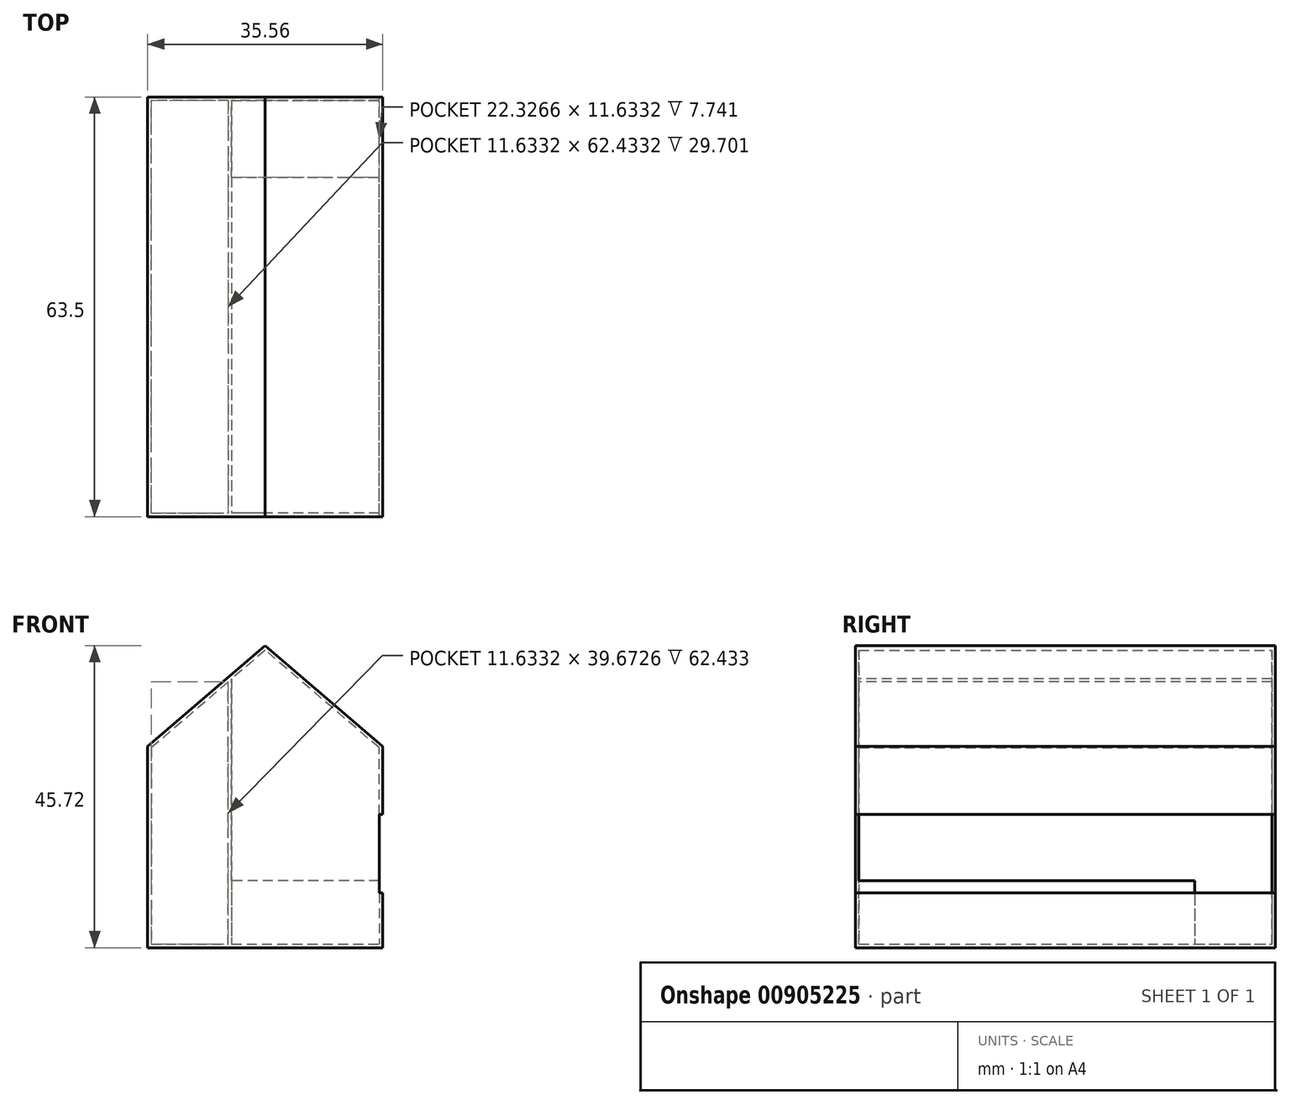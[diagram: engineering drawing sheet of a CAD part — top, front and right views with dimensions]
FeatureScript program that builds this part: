
annotation { "Feature Type Name" : "Feature", "Feature Type Description" : "" }
export const myFeature = defineFeature(function(context is Context, id is Id, definition is map)
    precondition{}
    {
        {
            var Q0;
            Q0=qCreatedBy(makeId("Front.planeOp"),FACE);
            var sketch = newSketch(context, id + "F0", { "sketchPlane" : qUnion([Q0])});
            skLineSegment(sketch, "E0", {"start": v(0, 0) * mm, "end": v(35.56, 0) * mm});
            skLineSegment(sketch, "E1", {"start": v(35.56, 0) * mm, "end": v(35.56, 8.27) * mm});
            skLineSegment(sketch, "E2", {"start": v(35.56, 30.48) * mm, "end": v(17.78, 45.72) * mm});
            skLineSegment(sketch, "E3", {"start": v(17.78, 45.72) * mm, "end": v(0, 30.48) * mm});
            skLineSegment(sketch, "E4", {"start": v(0, 30.48) * mm, "end": v(0, 0) * mm});
            skLineSegment(sketch, "E5.0", {"start": v(35.03, 30.23) * mm, "end": v(17.78, 45.02) * mm});
            skLineSegment(sketch, "E6.0", {"start": v(17.78, 45.02) * mm, "end": v(0.53, 30.23) * mm});
            skLineSegment(sketch, "E7.0", {"start": v(35.03, 0.53) * mm, "end": v(35.03, 8.27) * mm});
            skLineSegment(sketch, "E8.0", {"start": v(0.53, 30.23) * mm, "end": v(0.53, 0.53) * mm});
            skLineSegment(sketch, "E9.0", {"start": v(0.53, 0.53) * mm, "end": v(35.03, 0.53) * mm});
            skLineSegment(sketch, "E10", {"start": v(35.56, 8.27) * mm, "end": v(35.03, 8.27) * mm});
            skLineSegment(sketch, "E11", {"start": v(35.56, 20.14) * mm, "end": v(35.03, 20.14) * mm});
            skLineSegment(sketch, "E12.trimOffspring", {"start": v(35.03, 20.14) * mm, "end": v(35.03, 30.23) * mm});
            skLineSegment(sketch, "E13.trimOffspring", {"start": v(35.56, 20.14) * mm, "end": v(35.56, 30.48) * mm});
            skSolve(sketch);
        }
        {
            var Q0;
            Q0=makeQuery(id+"F0.imprint","IMPRINT",FACE,{"disambiguationData":[TD([[makeQuery(id+"F0.imprint","IMPRINT",EDGE,{"derivedFrom":sQuery(id+"F0.wireOp",EDGE,"E0")}),1.0]])]});
            extrude(context, id + "F1", {"entities" : qUnion([Q0]), "depth" : 63.5 * mm, "offsetDistance" : 25.4 * mm});
        }
        {
            var Q0;
            Q0=makeQuery(id+"F1.opExtrude","CAP_FACE",FACE,{"disambiguationData":[OSD([sQuery(id+"F0.wireOp",EDGE,"E0"),sQuery(id+"F0.wireOp",EDGE,"E1"),sQuery(id+"F0.wireOp",EDGE,"E2"),sQuery(id+"F0.wireOp",EDGE,"E3"),sQuery(id+"F0.wireOp",EDGE,"E4"),sQuery(id+"F0.wireOp",EDGE,"E5.0"),sQuery(id+"F0.wireOp",EDGE,"E6.0"),sQuery(id+"F0.wireOp",EDGE,"E7.0"),sQuery(id+"F0.wireOp",EDGE,"E8.0"),sQuery(id+"F0.wireOp",EDGE,"E9.0"),sQuery(id+"F0.wireOp",EDGE,"E10"),sQuery(id+"F0.wireOp",EDGE,"E11"),sQuery(id+"F0.wireOp",EDGE,"E12.trimOffspring"),sQuery(id+"F0.wireOp",EDGE,"E13.trimOffspring")])],"isStart":false});
            var sketch = newSketch(context, id + "F2", { "sketchPlane" : qUnion([Q0])});
            skLineSegment(sketch, "E14", {"start": v(35.03, 30.23) * mm, "end": v(17.78, 45.02) * mm});
            skLineSegment(sketch, "E15", {"start": v(17.78, 45.02) * mm, "end": v(0.53, 30.23) * mm});
            skLineSegment(sketch, "E16", {"start": v(0.53, 30.23) * mm, "end": v(0.53, 0.53) * mm});
            skLineSegment(sketch, "E17", {"start": v(0.53, 0.53) * mm, "end": v(35.03, 0.53) * mm});
            skLineSegment(sketch, "E18", {"start": v(35.03, 0.53) * mm, "end": v(35.03, 30.23) * mm});
            skSolve(sketch);
        }
        {
            var Q0;
            Q0 = qSketchRegion(id + "F2", true);
            extrude(context, id + "F3", {"entities" : qUnion([Q0]), "operationType" : NewBodyOperationType.ADD, "oppositeDirection" : true, "depth" : 0.53 * mm, "offsetDistance" : 25.4 * mm});
        }
        {
            var Q0;
            Q0=makeQuery(id+"F1.opExtrude","CAP_FACE",FACE,{"disambiguationData":[OSD([sQuery(id+"F0.wireOp",EDGE,"E0"),sQuery(id+"F0.wireOp",EDGE,"E1"),sQuery(id+"F0.wireOp",EDGE,"E2"),sQuery(id+"F0.wireOp",EDGE,"E3"),sQuery(id+"F0.wireOp",EDGE,"E4"),sQuery(id+"F0.wireOp",EDGE,"E5.0"),sQuery(id+"F0.wireOp",EDGE,"E6.0"),sQuery(id+"F0.wireOp",EDGE,"E7.0"),sQuery(id+"F0.wireOp",EDGE,"E8.0"),sQuery(id+"F0.wireOp",EDGE,"E9.0"),sQuery(id+"F0.wireOp",EDGE,"E10"),sQuery(id+"F0.wireOp",EDGE,"E11"),sQuery(id+"F0.wireOp",EDGE,"E12.trimOffspring"),sQuery(id+"F0.wireOp",EDGE,"E13.trimOffspring")])],"isStart":true});
            var sketch = newSketch(context, id + "F4", { "sketchPlane" : qUnion([Q0])});
            skLineSegment(sketch, "E19", {"start": v(-35.03, 0.53) * mm, "end": v(-35.03, 30.23) * mm});
            skLineSegment(sketch, "E20", {"start": v(-35.03, 30.23) * mm, "end": v(-17.78, 45.02) * mm});
            skLineSegment(sketch, "E21", {"start": v(-17.78, 45.02) * mm, "end": v(-0.53, 30.23) * mm});
            skLineSegment(sketch, "E22", {"start": v(-0.53, 30.23) * mm, "end": v(-0.53, 0.53) * mm});
            skLineSegment(sketch, "E23", {"start": v(-0.53, 0.53) * mm, "end": v(-35.03, 0.53) * mm});
            skSolve(sketch);
        }
        {
            var Q0;
            Q0 = qSketchRegion(id + "F4", true);
            extrude(context, id + "F5", {"entities" : qUnion([Q0]), "operationType" : NewBodyOperationType.ADD, "oppositeDirection" : true, "depth" : 0.53 * mm, "offsetDistance" : 25.4 * mm});
        }
        {
            var Q0;
            Q0=makeQuery(id+"F3.boolean.opBoolean","MERGE",FACE,{"derivedFrom":[makeQuery(id+"F1.opExtrude","CAP_FACE",FACE,{"disambiguationData":[OSD([sQuery(id+"F0.wireOp",EDGE,"E0"),sQuery(id+"F0.wireOp",EDGE,"E1"),sQuery(id+"F0.wireOp",EDGE,"E2"),sQuery(id+"F0.wireOp",EDGE,"E3"),sQuery(id+"F0.wireOp",EDGE,"E4"),sQuery(id+"F0.wireOp",EDGE,"E5.0"),sQuery(id+"F0.wireOp",EDGE,"E6.0"),sQuery(id+"F0.wireOp",EDGE,"E7.0"),sQuery(id+"F0.wireOp",EDGE,"E8.0"),sQuery(id+"F0.wireOp",EDGE,"E9.0"),sQuery(id+"F0.wireOp",EDGE,"E10"),sQuery(id+"F0.wireOp",EDGE,"E11"),sQuery(id+"F0.wireOp",EDGE,"E12.trimOffspring"),sQuery(id+"F0.wireOp",EDGE,"E13.trimOffspring")])],"isStart":false}),makeQuery(id+"F3.opExtrude","CAP_FACE",FACE,{"disambiguationData":[OSD([sQuery(id+"F2.wireOp",EDGE,"E14"),sQuery(id+"F2.wireOp",EDGE,"E15"),sQuery(id+"F2.wireOp",EDGE,"E16"),sQuery(id+"F2.wireOp",EDGE,"E17"),sQuery(id+"F2.wireOp",EDGE,"E18")])],"isStart":true})]});
            var sketch = newSketch(context, id + "F6", { "sketchPlane" : qUnion([Q0])});
            skLineSegment(sketch, "E24.bottom", {"start": v(12.17, 0) * mm, "end": v(12.7, 0) * mm});
            skLineSegment(sketch, "E24.left", {"start": v(12.7, 0) * mm, "end": v(12.7, 41.37) * mm});
            skLineSegment(sketch, "E24.right", {"start": v(12.17, 0) * mm, "end": v(12.17, 40.9) * mm});
            skLineSegment(sketch, "E25", {"start": v(12.17, 40.9) * mm, "end": v(12.7, 41.37) * mm});
            skPoint(sketch, "E24.top.end.orphan", {"position": v(12.17, 43.18) * mm});
            skSolve(sketch);
        }
        {
            var Q0;
            Q0=makeQuery(id+"F6.imprint","IMPRINT",FACE,{"disambiguationData":[TD([[makeQuery(id+"F6.imprint","IMPRINT",EDGE,{"derivedFrom":sQuery(id+"F6.wireOp",EDGE,"E24.bottom")}),1.0]])]});
            extrude(context, id + "F7", {"entities" : qUnion([Q0]), "operationType" : NewBodyOperationType.ADD, "oppositeDirection" : true, "depth" : 63.5 * mm, "offsetDistance" : 25.4 * mm});
        }
        {
            var Q0;
            Q0=qCreatedBy(makeId("Top.planeOp"),FACE);
            var sketch = newSketch(context, id + "F8", { "sketchPlane" : qUnion([Q0])});
            skLineSegment(sketch, "E26.bottom", {"start": v(35.03, -62.97) * mm, "end": v(12.17, -62.97) * mm});
            skLineSegment(sketch, "E26.top", {"start": v(35.03, -12.17) * mm, "end": v(12.17, -12.17) * mm});
            skLineSegment(sketch, "E26.left", {"start": v(35.03, -62.97) * mm, "end": v(35.03, -12.17) * mm});
            skLineSegment(sketch, "E26.right", {"start": v(12.17, -62.97) * mm, "end": v(12.17, -12.17) * mm});
            skSolve(sketch);
        }
        {
            var Q0;
            Q0 = qSketchRegion(id + "F8", true);
            extrude(context, id + "F9", {"entities" : qUnion([Q0]), "operationType" : NewBodyOperationType.ADD, "depth" : 10.16 * mm, "offsetDistance" : 25.4 * mm});
        }
    });
